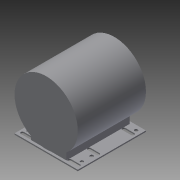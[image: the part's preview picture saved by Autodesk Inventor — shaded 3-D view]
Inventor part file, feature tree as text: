
AUTODESK INVENTOR PART (.ipt)
format: ipt  version: 2015 SP1 (Build 190203100, 203)  size: 202,240 bytes
history: native  units: in
note: dims shown in document units (in); Inventor stores cm internally (conversion verified against a paired STEP export)
features: sketch x7, extrude x5, plane x3, hole x1, projected_geometry x1
ambient origin geometry x8: Origin, YZ Plane, XZ Plane, XY Plane, X Axis, Y Axis, Z Axis, Center Point
bodies: Solid1 (feature_tree)
feature tree (17):
  extrude  "Extrusion1"  Depth=0.1in
  extrude  "Extrusion2"  Depth=2.0in
  hole  "Hole1"  [1 undecoded]
  plane  "Work Plane2"
  extrude  "Extrusion3"  TaperAngle=0.0deg  [1 undecoded]
  plane  "Work Plane7"
  extrude  "Extrusion4"  TaperAngle=45.0deg  [1 undecoded]
  plane  "Work Plane9"
  extrude  "Extrusion5"  TaperAngle=135.0deg  [1 undecoded]
  sketch  "Sketch7"  dims[d12=135.0deg d13=0.196in d14=0.5in d15=0.375in d16=0.25in d17=0.5635in d18=0.75in d19=0.8108in d20=6.5in d21=0.25in d22=3.65in d23=1.0in d24=0.0in d27=0.206in d28=0.0in d29=0.125in d30=0.0in d31=0.333in d32=0.5115in d33=0.9355in d38=0.333in d39=0.333in d40=0.902in d41=0.333in d46=0.266in d47=0.3665in d50=0.4975in d51=0.3365in d52=0.25in d53=0.0in]
  sketch  "Sketch1"  dims[d0=0.625in d1=0.1in]
  sketch  "Sketch2"  dims[d2=0.191in d3=2.0in]
  sketch  "Sketch3"  dims[d4=0.0in d5=6.5in]
  sketch  "Sketch4"  dims[d6=7.0in d7=0.0in]
  projected_geometry  "Projected Loop1"
  sketch  "Sketch5"  dims[d8=5.75in d9=45.0deg]
  sketch  "Sketch6"  dims[d10=45.0deg d11=135.0deg]
note: 4 required parameter values undecoded (feature->parameter linkage not recoverable at this tier; creation-order binding heuristic only, values carry confidence <= 0.55)
